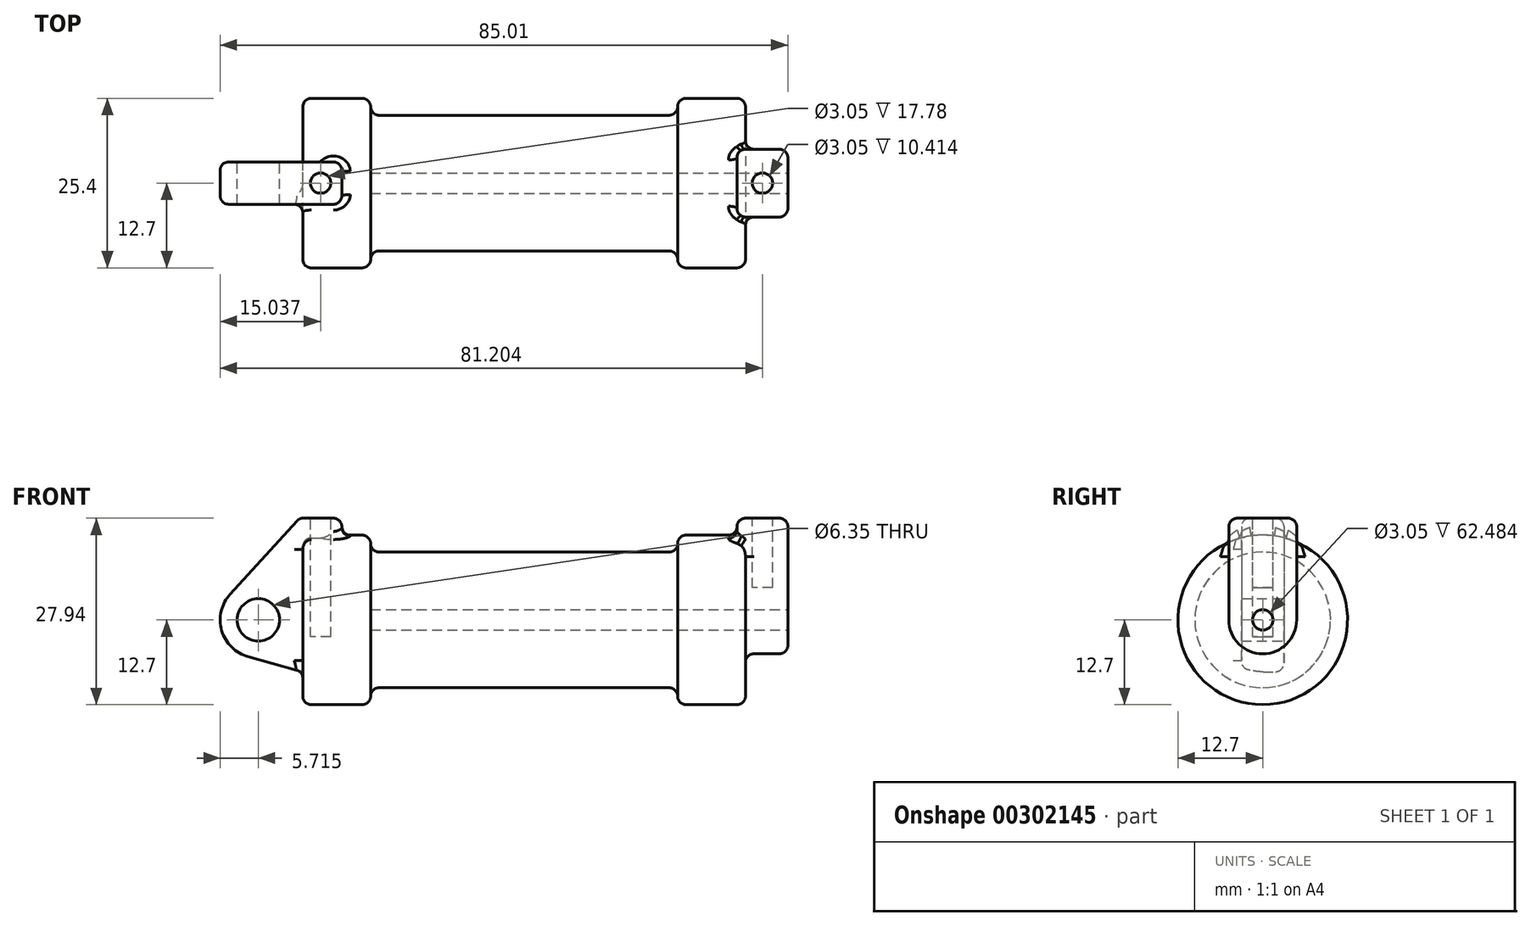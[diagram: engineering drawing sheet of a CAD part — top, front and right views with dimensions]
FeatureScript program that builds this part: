
annotation { "Feature Type Name" : "Feature", "Feature Type Description" : "" }
export const myFeature = defineFeature(function(context is Context, id is Id, definition is map)
    precondition{}
    {
        {
            var Q0;
            Q0=qCreatedBy(makeId("Front.planeOp"),FACE);
            var sketch = newSketch(context, id + "F0", { "sketchPlane" : qUnion([Q0])});
            skLineSegment(sketch, "E0", {"start": v(0, 0) * mm, "end": v(0, 12.7) * mm});
            skLineSegment(sketch, "E1", {"start": v(0, 12.7) * mm, "end": v(10.16, 12.7) * mm});
            skLineSegment(sketch, "E2", {"start": v(10.16, 12.7) * mm, "end": v(10.16, 10.16) * mm});
            skLineSegment(sketch, "E3", {"start": v(10.16, 10.16) * mm, "end": v(56.13, 10.16) * mm});
            skLineSegment(sketch, "E4", {"start": v(56.13, 10.16) * mm, "end": v(56.13, 12.7) * mm});
            skLineSegment(sketch, "E5", {"start": v(56.13, 12.7) * mm, "end": v(66.3, 12.7) * mm});
            skLineSegment(sketch, "E6", {"start": v(66.3, 12.7) * mm, "end": v(66.3, 0) * mm});
            skLineSegment(sketch, "E7", {"start": v(66.3, 0) * mm, "end": v(0, 0) * mm});
            skLineSegment(sketch, "E8", {"start": v(5.84, 15.24) * mm, "end": v(-0.5, 15.24) * mm});
            skLineSegment(sketch, "E9", {"start": v(-0.5, 15.24) * mm, "end": v(-10.88, 3.85) * mm});
            skLineSegment(sketch, "E10", {"start": v(0, 0) * mm, "end": v(-6.65, 0) * mm});
            skCircle(sketch, "E11", {"center": v(-6.65, 0) * mm, "radius": 5.72 * mm});
            skCircle(sketch, "E12", {"center": v(-6.65, 0) * mm, "radius": 3.18 * mm});
            skLineSegment(sketch, "E13", {"start": v(5.84, 15.24) * mm, "end": v(5.84, -9.4) * mm});
            skLineSegment(sketch, "E14", {"start": v(5.84, -9.4) * mm, "end": v(-8.18, -5.5) * mm});
            skSolve(sketch);
        }
        {
            var Q0;
            {var subQ0=sQuery(id+"F0.wireOp",EDGE,"E0");Q0=makeQuery(id+"F0.imprint","IMPRINT",FACE,{"disambiguationData":[TD([[makeQuery(id+"F0.imprint","IMPRINT",EDGE,{"derivedFrom":subQ0}),-1.0]])]});}
            var Q1;
            {var subQ0=sQuery(id+"F0.wireOp",EDGE,"E2");Q1=makeQuery(id+"F0.imprint","IMPRINT",FACE,{"disambiguationData":[TD([[makeQuery(id+"F0.imprint","IMPRINT",EDGE,{"derivedFrom":subQ0}),-1.0]])]});}
            var Q2;
            Q2=sQuery(id+"F0.wireOp",EDGE,"E7");
            revolve(context, id + "F1", {"entities" : qUnion([Q0, Q1]), "axis" : qUnion([Q2]), "revolveType" : RevolveType.FULL});
        }
        {
            var Q0;
            {var subQ1=sQuery(id+"F0.wireOp",EDGE,"E0");Q0=makeQuery(id+"F0.imprint","IMPRINT",FACE,{"disambiguationData":[TD([[makeQuery(id+"F0.imprint","IMPRINT",EDGE,{"derivedFrom":subQ1}),1.0]])]});}
            var Q1;
            {var subQ0=sQuery(id+"F0.wireOp",EDGE,"E0");Q1=makeQuery(id+"F0.imprint","IMPRINT",FACE,{"disambiguationData":[TD([[makeQuery(id+"F0.imprint","IMPRINT",EDGE,{"derivedFrom":subQ0}),-1.0]])]});}
            var Q2;
            Q2=makeQuery(id+"F0.imprint","IMPRINT",FACE,{"disambiguationData":[TD([[makeQuery(id+"F0.imprint","IMPRINT",EDGE,{"derivedFrom":sQuery(id+"F0.wireOp",EDGE,"E12")}),-1.0]])]});
            var Q3;
            {var subQ0=sQuery(id+"F0.wireOp",EDGE,"E14");Q3=makeQuery(id+"F0.imprint","IMPRINT",FACE,{"disambiguationData":[TD([[makeQuery(id+"F0.imprint","IMPRINT",EDGE,{"derivedFrom":subQ0}),-1.0]])]});}
            extrude(context, id + "F2", {"entities" : qUnion([Q0, Q1, Q2, Q3]), "operationType" : NewBodyOperationType.ADD, "endBound" : BoundingType.SYMMETRIC, "depth" : 6.35 * mm});
        }
        {
            var Q0;
            Q0=makeQuery(id+"F1.opRevolve","SWEPT_FACE",FACE,{"disambiguationData":[OSD([sQuery(id+"F0.wireOp",EDGE,"E6")])]});
            var sketch = newSketch(context, id + "F3", { "sketchPlane" : qUnion([Q0])});
            skCircle(sketch, "E15", {"center": v(0, 0) * mm, "radius": 1.52 * mm});
            skCircle(sketch, "E16", {"center": v(0, 0) * mm, "radius": 5.08 * mm});
            skLineSegment(sketch, "E17", {"start": v(5.08, 0) * mm, "end": v(5.08, 15.24) * mm});
            skLineSegment(sketch, "E18.MirrorCS", {"start": v(-5.08, 0) * mm, "end": v(-5.08, 15.24) * mm});
            skLineSegment(sketch, "E19", {"start": v(-5.08, 15.24) * mm, "end": v(5.08, 15.24) * mm});
            skSolve(sketch);
        }
        {
            var Q0;
            {var subQ0=sQuery(id+"F3.wireOp",EDGE,"E19");Q0=makeQuery(id+"F3.imprint","IMPRINT",FACE,{"disambiguationData":[TD([[makeQuery(id+"F3.imprint","IMPRINT",EDGE,{"derivedFrom":subQ0}),-1.0]])]});}
            var Q1;
            Q1=makeQuery(id+"F3.imprint","IMPRINT",FACE,{"disambiguationData":[TD([[makeQuery(id+"F3.imprint","IMPRINT",EDGE,{"derivedFrom":sQuery(id+"F3.wireOp",EDGE,"E15")}),-1.0]])]});
            var Q2;
            {var subQ0=sQuery(id+"F3.wireOp",EDGE,"E17");var subQ1=sQuery(id+"F3.wireOp",EDGE,"E16");var subQ2=makeQuery(id+"F3.imprint","INTERSECT",VERTEX,{"derivedFrom":[subQ1,subQ0]});Q2=makeQuery(id+"F3.imprint","IMPRINT",FACE,{"disambiguationData":[TD([[makeQuery(id+"F3.imprint","IMPRINT",EDGE,{"disambiguationData":[TD([[subQ2,-1.0]])],"derivedFrom":subQ1}),-1.0]])]});}
            extrude(context, id + "F4", {"entities" : qUnion([Q0, Q1, Q2]), "operationType" : NewBodyOperationType.ADD, "oppositeDirection" : true, "depth" : 1.27 * mm, "hasSecondDirection" : true, "secondDirectionOppositeDirection" : false, "secondDirectionDepth" : 6.35 * mm});
        }
        {
            var Q0;
            Q0=makeQuery(id+"F3.imprint","IMPRINT",FACE,{"disambiguationData":[TD([[makeQuery(id+"F3.imprint","IMPRINT",EDGE,{"derivedFrom":sQuery(id+"F3.wireOp",EDGE,"E15")}),1.0]])]});
            var Q1;
            Q1=sQuery(id+"F3.wireOp",EDGE,"E15");
            var Q2;
            Q2=makeQuery(id+"F1.opRevolve","SWEPT_FACE",FACE,{"disambiguationData":[OSD([sQuery(id+"F0.wireOp",EDGE,"E2")])]});
            extrude(context, id + "F5", {"entities" : qUnion([Q0]), "operationType" : NewBodyOperationType.REMOVE, "surfaceEntities" : qUnion([Q1]), "endBound" : BoundingType.UP_TO_SURFACE, "oppositeDirection" : true, "endBoundEntityFace" : qUnion([Q2]), "depth" : 25.4 * mm});
        }
        {
            var Q0;
            Q0=makeQuery(id+"F2.opExtrude","SWEPT_FACE",FACE,{"disambiguationData":[OSD([sQuery(id+"F0.wireOp",EDGE,"E8")])]});
            var Q1;
            Q1=makeQuery(id+"F4.opExtrude","SWEPT_FACE",FACE,{"disambiguationData":[OSD([sQuery(id+"F3.wireOp",EDGE,"E19")])]});
            cPlane(context, id + "F6", {"entities" : qUnion([Q0, Q1]), "cplaneType" : CPlaneType.MID_PLANE, "offset" : 25.4 * mm, "width" : 152.4 * mm, "height" : 152.4 * mm});
        }
        {
            var Q0;
            Q0=qCreatedBy(id+"F6.planeOp",FACE);
            var sketch = newSketch(context, id + "F7", { "sketchPlane" : qUnion([Q0])});
            skCircle(sketch, "E20", {"center": v(2.67, 0) * mm, "radius": 1.52 * mm});
            skCircle(sketch, "E21", {"center": v(68.83, 0) * mm, "radius": 1.52 * mm});
            skSolve(sketch);
        }
        {
            var Q0;
            Q0=makeQuery(id+"F7.imprint","IMPRINT",FACE,{"disambiguationData":[TD([[makeQuery(id+"F7.imprint","IMPRINT",EDGE,{"derivedFrom":sQuery(id+"F7.wireOp",EDGE,"E20")}),1.0]])]});
            extrude(context, id + "F8", {"entities" : qUnion([Q0]), "operationType" : NewBodyOperationType.REMOVE, "oppositeDirection" : true, "depth" : 17.78 * mm});
        }
        {
            var Q0;
            Q0=makeQuery(id+"F7.imprint","IMPRINT",FACE,{"disambiguationData":[TD([[makeQuery(id+"F7.imprint","IMPRINT",EDGE,{"derivedFrom":sQuery(id+"F7.wireOp",EDGE,"E21")}),1.0]])]});
            var Q1;
            Q1=sQuery(id+"F7.wireOp",EDGE,"E21");
            extrude(context, id + "F9", {"entities" : qUnion([Q0]), "operationType" : NewBodyOperationType.REMOVE, "surfaceEntities" : qUnion([Q1]), "oppositeDirection" : true, "depth" : 10.4 * mm});
        }
        {
            var Q0;
            Q0=makeQuery(id+"F1.opRevolve","SWEPT_EDGE",EDGE,{"disambiguationData":[OSD([sQuery(id+"F0.wireOp",EDGE,"E1"),sQuery(id+"F0.wireOp",EDGE,"E2")])]});
            var Q1;
            Q1=makeQuery(id+"F1.opRevolve","SWEPT_EDGE",EDGE,{"disambiguationData":[OSD([sQuery(id+"F0.wireOp",EDGE,"E4"),sQuery(id+"F0.wireOp",EDGE,"E5")])]});
            var Q2;
            Q2=makeQuery(id+"F1.opRevolve","SWEPT_EDGE",EDGE,{"disambiguationData":[OSD([sQuery(id+"F0.wireOp",EDGE,"E2"),sQuery(id+"F0.wireOp",EDGE,"E3")])]});
            var Q3;
            Q3=makeQuery(id+"F1.opRevolve","SWEPT_EDGE",EDGE,{"disambiguationData":[OSD([sQuery(id+"F0.wireOp",EDGE,"E3"),sQuery(id+"F0.wireOp",EDGE,"E4")])]});
            var Q4;
            Q4=makeQuery(id+"F1.opRevolve","SWEPT_EDGE",EDGE,{"disambiguationData":[OSD([sQuery(id+"F0.wireOp",EDGE,"E5"),sQuery(id+"F0.wireOp",EDGE,"E6")])]});
            var Q5;
            Q5=makeQuery(id+"F1.opRevolve","SWEPT_EDGE",EDGE,{"disambiguationData":[OSD([sQuery(id+"F0.wireOp",EDGE,"E0"),sQuery(id+"F0.wireOp",EDGE,"E1")])]});
            fillet(context, id + "F10", {"entities" : qUnion([Q0, Q1, Q2, Q3, Q4, Q5]), "radius" : 1.27 * mm, "tangentPropagation" : true, "allowEdgeOverflow" : false});
        }
        {
            var Q0;
            Q0=makeQuery(id+"F2.opExtrude","CAP_EDGE",EDGE,{"disambiguationData":[OSD([sQuery(id+"F0.wireOp",EDGE,"E9")])],"isStart":false});
            var Q1;
            Q1=makeQuery(id+"F2.opExtrude","CAP_EDGE",EDGE,{"disambiguationData":[OSD([sQuery(id+"F0.wireOp",EDGE,"E9")])],"isStart":true});
            var Q2;
            Q2=makeQuery(id+"F2.opExtrude","SWEPT_EDGE",EDGE,{"disambiguationData":[OSD([sQuery(id+"F0.wireOp",EDGE,"E8"),sQuery(id+"F0.wireOp",EDGE,"E9")])]});
            var Q3;
            Q3=makeQuery(id+"F2.opExtrude","CAP_EDGE",EDGE,{"disambiguationData":[OSD([sQuery(id+"F0.wireOp",EDGE,"E8")])],"isStart":false});
            var Q4;
            Q4=makeQuery(id+"F2.opExtrude","SWEPT_EDGE",EDGE,{"disambiguationData":[OSD([sQuery(id+"F0.wireOp",EDGE,"E8"),sQuery(id+"F0.wireOp",EDGE,"E13")])]});
            var Q5;
            Q5=makeQuery(id+"F2.boolean.opBoolean","INTERSECT",EDGE,{"derivedFrom":[makeQuery(id+"F1.opRevolve","SWEPT_FACE",FACE,{"disambiguationData":[OSD([sQuery(id+"F0.wireOp",EDGE,"E1")])]}),makeQuery(id+"F2.opExtrude","CAP_FACE",FACE,{"disambiguationData":[OSD([sQuery(id+"F0.wireOp",EDGE,"E8"),sQuery(id+"F0.wireOp",EDGE,"E9"),sQuery(id+"F0.wireOp",EDGE,"E11"),sQuery(id+"F0.wireOp",EDGE,"E12"),sQuery(id+"F0.wireOp",EDGE,"E13"),sQuery(id+"F0.wireOp",EDGE,"E14")])],"isStart":false})]});
            var Q6;
            Q6=makeQuery(id+"F2.boolean.opBoolean","INTERSECT",EDGE,{"derivedFrom":[makeQuery(id+"F1.opRevolve","SWEPT_FACE",FACE,{"disambiguationData":[OSD([sQuery(id+"F0.wireOp",EDGE,"E1")])]}),makeQuery(id+"F2.opExtrude","SWEPT_FACE",FACE,{"disambiguationData":[OSD([sQuery(id+"F0.wireOp",EDGE,"E13")])]})]});
            var Q7;
            Q7=makeQuery(id+"F2.opExtrude","CAP_EDGE",EDGE,{"disambiguationData":[OSD([sQuery(id+"F0.wireOp",EDGE,"E13")])],"isStart":true});
            var Q8;
            Q8=makeQuery(id+"F2.opExtrude","CAP_EDGE",EDGE,{"disambiguationData":[OSD([sQuery(id+"F0.wireOp",EDGE,"E13")])],"isStart":false});
            var Q9;
            Q9=makeQuery(id+"F2.opExtrude","CAP_EDGE",EDGE,{"disambiguationData":[OSD([sQuery(id+"F0.wireOp",EDGE,"E8")])],"isStart":true});
            fillet(context, id + "F11", {"entities" : qUnion([Q0, Q1, Q2, Q3, Q4, Q5, Q6, Q7, Q8, Q9]), "radius" : 1.27 * mm, "tangentPropagation" : true, "allowEdgeOverflow" : false});
        }
        {
            var Q0;
            Q0=makeQuery(id+"F4.opExtrude","CAP_EDGE",EDGE,{"disambiguationData":[OSD([sQuery(id+"F3.wireOp",EDGE,"E19")])],"isStart":true});
            var Q1;
            Q1=makeQuery(id+"F4.opExtrude","CAP_EDGE",EDGE,{"disambiguationData":[OSD([sQuery(id+"F3.wireOp",EDGE,"E19")])],"isStart":false});
            var Q2;
            Q2=makeQuery(id+"F4.opExtrude","SWEPT_EDGE",EDGE,{"disambiguationData":[OSD([sQuery(id+"F3.wireOp",EDGE,"E17"),sQuery(id+"F3.wireOp",EDGE,"E19")])]});
            var Q3;
            Q3=makeQuery(id+"F4.opExtrude","SWEPT_EDGE",EDGE,{"disambiguationData":[OSD([sQuery(id+"F3.wireOp",EDGE,"E18.MirrorCS"),sQuery(id+"F3.wireOp",EDGE,"E19")])]});
            var Q4;
            Q4=makeQuery(id+"F4.opExtrude","CAP_EDGE",EDGE,{"disambiguationData":[OSD([sQuery(id+"F3.wireOp",EDGE,"E18.MirrorCS")])],"isStart":true});
            var Q5;
            Q5=makeQuery(id+"F4.opExtrude","CAP_EDGE",EDGE,{"disambiguationData":[OSD([sQuery(id+"F3.wireOp",EDGE,"E17")])],"isStart":true});
            var Q6;
            Q6=makeQuery(id+"F4.opExtrude","CAP_EDGE",EDGE,{"disambiguationData":[OSD([sQuery(id+"F3.wireOp",EDGE,"E16")])],"isStart":true});
            var Q7;
            Q7=makeQuery(id+"F4.boolean.opBoolean","INTERSECT",EDGE,{"derivedFrom":[makeQuery(id+"F1.opRevolve","SWEPT_FACE",FACE,{"disambiguationData":[OSD([sQuery(id+"F0.wireOp",EDGE,"E6")])]}),makeQuery(id+"F4.opExtrude","SWEPT_FACE",FACE,{"disambiguationData":[OSD([sQuery(id+"F3.wireOp",EDGE,"E17")])]})]});
            var Q8;
            Q8=makeQuery(id+"F4.boolean.opBoolean","INTERSECT",EDGE,{"derivedFrom":[makeQuery(id+"F1.opRevolve","SWEPT_FACE",FACE,{"disambiguationData":[OSD([sQuery(id+"F0.wireOp",EDGE,"E5")])]}),makeQuery(id+"F4.opExtrude","CAP_FACE",FACE,{"disambiguationData":[OSD([sQuery(id+"F3.wireOp",EDGE,"E15"),sQuery(id+"F3.wireOp",EDGE,"E16"),sQuery(id+"F3.wireOp",EDGE,"E17"),sQuery(id+"F3.wireOp",EDGE,"E18.MirrorCS"),sQuery(id+"F3.wireOp",EDGE,"E19")])],"isStart":false})]});
            var Q9;
            Q9=makeQuery(id+"F4.opExtrude","CAP_EDGE",EDGE,{"disambiguationData":[OSD([sQuery(id+"F3.wireOp",EDGE,"E17")])],"isStart":false});
            var Q10;
            Q10=makeQuery(id+"F4.opExtrude","CAP_EDGE",EDGE,{"disambiguationData":[OSD([sQuery(id+"F3.wireOp",EDGE,"E18.MirrorCS")])],"isStart":false});
            var Q11;
            Q11=makeQuery(id+"F4.boolean.opBoolean","INTERSECT",EDGE,{"derivedFrom":[makeQuery(id+"F1.opRevolve","SWEPT_FACE",FACE,{"disambiguationData":[OSD([sQuery(id+"F0.wireOp",EDGE,"E6")])]}),makeQuery(id+"F4.opExtrude","SWEPT_FACE",FACE,{"disambiguationData":[OSD([sQuery(id+"F3.wireOp",EDGE,"E16")])]})]});
            fillet(context, id + "F12", {"entities" : qUnion([Q0, Q1, Q2, Q3, Q4, Q5, Q6, Q7, Q8, Q9, Q10, Q11]), "radius" : 1.27 * mm, "tangentPropagation" : true, "allowEdgeOverflow" : false});
        }
    });
